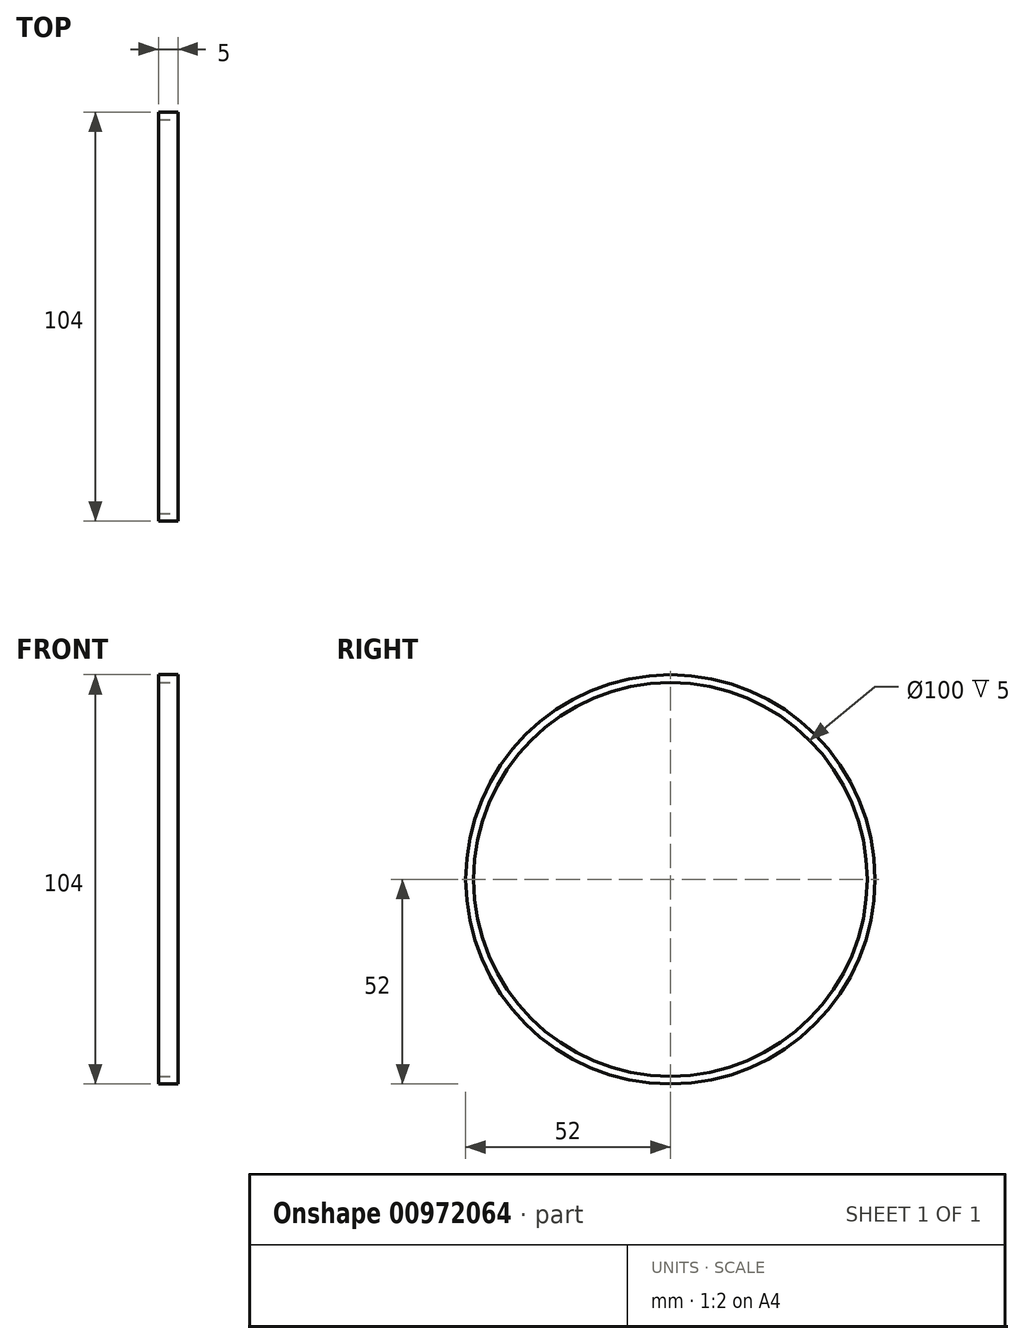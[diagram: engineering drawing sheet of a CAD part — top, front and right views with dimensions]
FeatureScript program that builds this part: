
annotation { "Feature Type Name" : "Feature", "Feature Type Description" : "" }
export const myFeature = defineFeature(function(context is Context, id is Id, definition is map)
    precondition{}
    {
        {
            var Q0;
            Q0=qCreatedBy(makeId("Front.planeOp"),FACE);
            var sketch = newSketch(context, id + "F0", { "sketchPlane" : qUnion([Q0])});
            skLineSegment(sketch, "E0", {"start": v(0, 0) * mm, "end": v(-79.76, 0) * mm, "construction": true});
            skLineSegment(sketch, "E1", {"start": v(0, 52) * mm, "end": v(-5, 52) * mm});
            skLineSegment(sketch, "E2", {"start": v(-5, 52) * mm, "end": v(-5, 50) * mm});
            skLineSegment(sketch, "E3", {"start": v(-5, 50) * mm, "end": v(0, 50) * mm});
            skLineSegment(sketch, "E4", {"start": v(0, 50) * mm, "end": v(0, 52) * mm});
            skSolve(sketch);
        }
        {
            var Q0;
            Q0 = qSketchRegion(id + "F0", true);
            var Q1;
            Q1=sQuery(id+"F0.wireOp",EDGE,"E0");
            revolve(context, id + "F1", {"surfaceOperationType" : NewSurfaceOperationType.NEW, "entities" : qUnion([Q0]), "axis" : qUnion([Q1]), "revolveType" : RevolveType.FULL});
        }
    });
